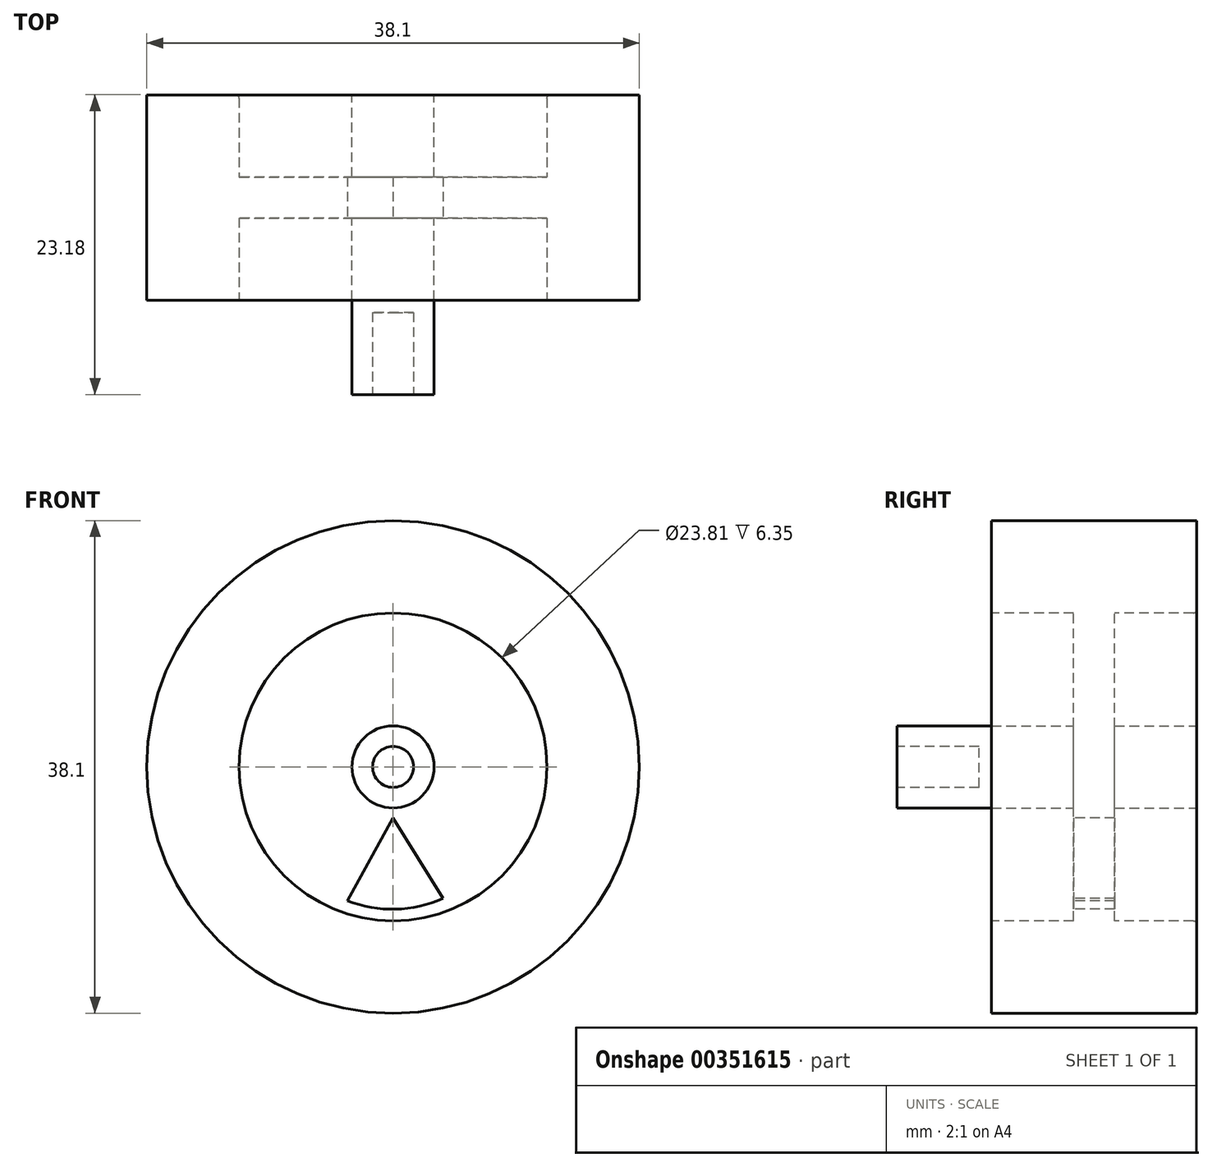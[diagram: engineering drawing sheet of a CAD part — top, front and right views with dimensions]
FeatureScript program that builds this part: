
annotation { "Feature Type Name" : "Feature", "Feature Type Description" : "" }
export const myFeature = defineFeature(function(context is Context, id is Id, definition is map)
    precondition{}
    {
        {
            var Q0;
            Q0=qCreatedBy(makeId("Front.planeOp"),FACE);
            var sketch = newSketch(context, id + "F0", { "sketchPlane" : qUnion([Q0])});
            skCircle(sketch, "E0", {"center": v(0, 0) * mm, "radius": 19.05 * mm});
            skSolve(sketch);
        }
        {
            var Q0;
            Q0 = qSketchRegion(id + "F0", true);
            extrude(context, id + "F1", {"entities" : qUnion([Q0]), "depth" : 15.88 * mm, "symmetric" : true});
        }
        {
            var Q0;
            Q0=qCreatedBy(makeId("Front.planeOp"),FACE);
            var sketch = newSketch(context, id + "F2", { "sketchPlane" : qUnion([Q0])});
            skCircle(sketch, "E1", {"center": v(0, 0) * mm, "radius": 11.9 * mm});
            skSolve(sketch);
        }
        {
            var Q0;
            Q0 = qSketchRegion(id + "F2", true);
            extrude(context, id + "F3", {"entities" : qUnion([Q0]), "operationType" : NewBodyOperationType.REMOVE, "endBound" : BoundingType.THROUGH_ALL, "oppositeDirection" : true, "depth" : 25.4 * mm, "hasSecondDirection" : true, "secondDirectionOppositeDirection" : false, "secondDirectionDepth" : 25.4 * mm});
        }
        {
            var Q0;
            Q0=qCreatedBy(makeId("Front.planeOp"),FACE);
            var sketch = newSketch(context, id + "F4", { "sketchPlane" : qUnion([Q0])});
            skCircle(sketch, "E2", {"center": v(0, 0) * mm, "radius": 11.9 * mm});
            skSolve(sketch);
        }
        {
            var Q0;
            Q0 = qSketchRegion(id + "F4", true);
            extrude(context, id + "F5", {"entities" : qUnion([Q0]), "operationType" : NewBodyOperationType.ADD, "depth" : 3.17 * mm, "symmetric" : true});
        }
        {
            var Q0;
            Q0=qCreatedBy(makeId("Front.planeOp"),FACE);
            var sketch = newSketch(context, id + "F6", { "sketchPlane" : qUnion([Q0])});
            skCircle(sketch, "E3", {"center": v(0, 0) * mm, "radius": 3.18 * mm});
            skSolve(sketch);
        }
        {
            var Q0;
            Q0 = qSketchRegion(id + "F6", true);
            extrude(context, id + "F7", {"entities" : qUnion([Q0]), "operationType" : NewBodyOperationType.ADD, "depth" : 15.24 * mm, "hasSecondDirection" : true, "secondDirectionOppositeDirection" : true, "secondDirectionDepth" : 7.94 * mm});
        }
        {
            var Q0;
            Q0=makeQuery(id+"F3.boolean.opBoolean","INTERSECT",EDGE,{"derivedFrom":[makeQuery(id+"F1.opExtrude","CAP_FACE",FACE,{"disambiguationData":[OSD([sQuery(id+"F0.wireOp",EDGE,"E0")])],"isStart":true}),makeQuery(id+"F3.opExtrude","SWEPT_FACE",FACE,{"disambiguationData":[OSD([sQuery(id+"F2.wireOp",EDGE,"E1")])]})]});
            fillet(context, id + "F8", {"entities" : qUnion([Q0]), "radius" : 0.25 * mm, "tangentPropagation" : true, "allowEdgeOverflow" : false});
        }
        {
            var Q0;
            Q0=makeQuery(id+"F5.opExtrude","CAP_FACE",FACE,{"disambiguationData":[OSD([sQuery(id+"F4.wireOp",EDGE,"E2")])],"isStart":false});
            var sketch = newSketch(context, id + "F9", { "sketchPlane" : qUnion([Q0])});
            skLineSegment(sketch, "E4", {"start": v(0, -3.95) * mm, "end": v(3.87, -10.17) * mm});
            skLineSegment(sketch, "E5", {"start": v(0, -3.95) * mm, "end": v(-3.54, -10.36) * mm});
            skArc(sketch, "E6", {"start": v(-3.54, -10.36) * mm, "mid": v(0.19, -11) * mm, "end": v(3.87, -10.17) * mm});
            skSolve(sketch);
        }
        {
            var Q0;
            Q0=makeQuery(id+"F9.imprint","IMPRINT",FACE,{"disambiguationData":[TD([[makeQuery(id+"F9.imprint","IMPRINT",EDGE,{"derivedFrom":sQuery(id+"F9.wireOp",EDGE,"E4")}),-1.0]])]});
            extrude(context, id + "F10", {"entities" : qUnion([Q0]), "operationType" : NewBodyOperationType.REMOVE, "oppositeDirection" : true, "depth" : 25.4 * mm, "symmetric" : true});
        }
        {
            var Q0;
            Q0=makeQuery(id+"F7.opExtrude","CAP_FACE",FACE,{"disambiguationData":[OSD([sQuery(id+"F6.wireOp",EDGE,"E3")])],"isStart":false});
            var sketch = newSketch(context, id + "F11", { "sketchPlane" : qUnion([Q0])});
            skCircle(sketch, "E7", {"center": v(0, 0) * mm, "radius": 1.59 * mm});
            skSolve(sketch);
        }
        {
            var Q0;
            Q0 = qSketchRegion(id + "F11", true);
            extrude(context, id + "F12", {"entities" : qUnion([Q0]), "operationType" : NewBodyOperationType.REMOVE, "oppositeDirection" : true, "depth" : 6.35 * mm});
        }
    });
